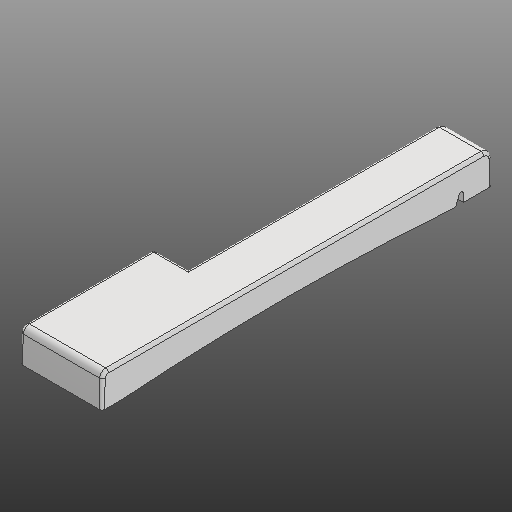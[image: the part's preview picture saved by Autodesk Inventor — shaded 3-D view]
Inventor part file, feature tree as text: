
AUTODESK INVENTOR PART (.ipt)
format: ipt  version: 2020 (Build 240168000, 168)  size: 317,952 bytes
history: native  units: in
note: dims shown in document units (in); Inventor stores cm internally (conversion verified against a paired STEP export)
features: extrude x4, other x3, fillet x2
ambient origin geometry x8: Origin, YZ Plane, XZ Plane, XY Plane, X Axis, Y Axis, Z Axis, Center Point
bodies: Solid1 (feature_tree)
feature tree (9):
  other  "Slot Start Plane"
  other  "Key Profile"
  extrude  "Upper (u)"  TaperAngle=0.0deg  [1 undecoded]
  extrude  "Lower (d)"  TaperAngle=0.0deg  [1 undecoded]
  extrude  "Protrusion Cutout"  Depth=0.0591in
  fillet  "Front Fillet"  Radius=0.1374in
  extrude  "Slot"  [1 undecoded]
  fillet  "Edge Softening"  Radius=0.0787in
  other  "Slot Sketch"
note: 3 required parameter values undecoded (feature->parameter linkage not recoverable at this tier; creation-order binding heuristic only, values carry confidence <= 0.55)
